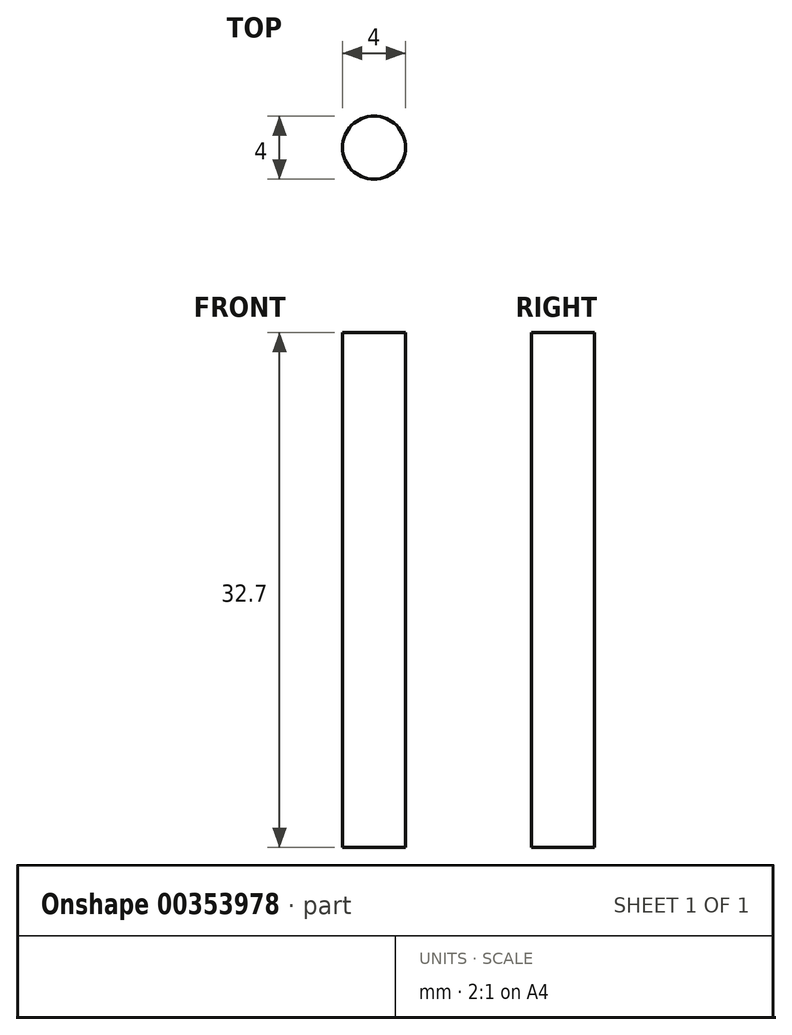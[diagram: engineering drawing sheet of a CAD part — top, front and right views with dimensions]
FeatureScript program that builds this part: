
annotation { "Feature Type Name" : "Feature", "Feature Type Description" : "" }
export const myFeature = defineFeature(function(context is Context, id is Id, definition is map)
    precondition{}
    {
        {
            var Q0;
            Q0=qCreatedBy(makeId("Top.planeOp"),FACE);
            var sketch = newSketch(context, id + "F0", { "sketchPlane" : qUnion([Q0])});
            skCircle(sketch, "E0", {"center": v(0, 0) * mm, "radius": 2 * mm});
            skSolve(sketch);
        }
        {
            var Q0;
            Q0 = qSketchRegion(id + "F0", true);
            var Q1;
            Q1=makeQuery(id+"F0.imprint","IMPRINT",FACE,{"disambiguationData":[TD([[makeQuery(id+"F0.imprint","IMPRINT",EDGE,{"derivedFrom":sQuery(id+"F0.wireOp",EDGE,"E0")}),1.0]])]});
            extrude(context, id + "F1", {"entities" : qUnion([Q0, Q1]), "depth" : 32.7 * mm});
        }
    });
